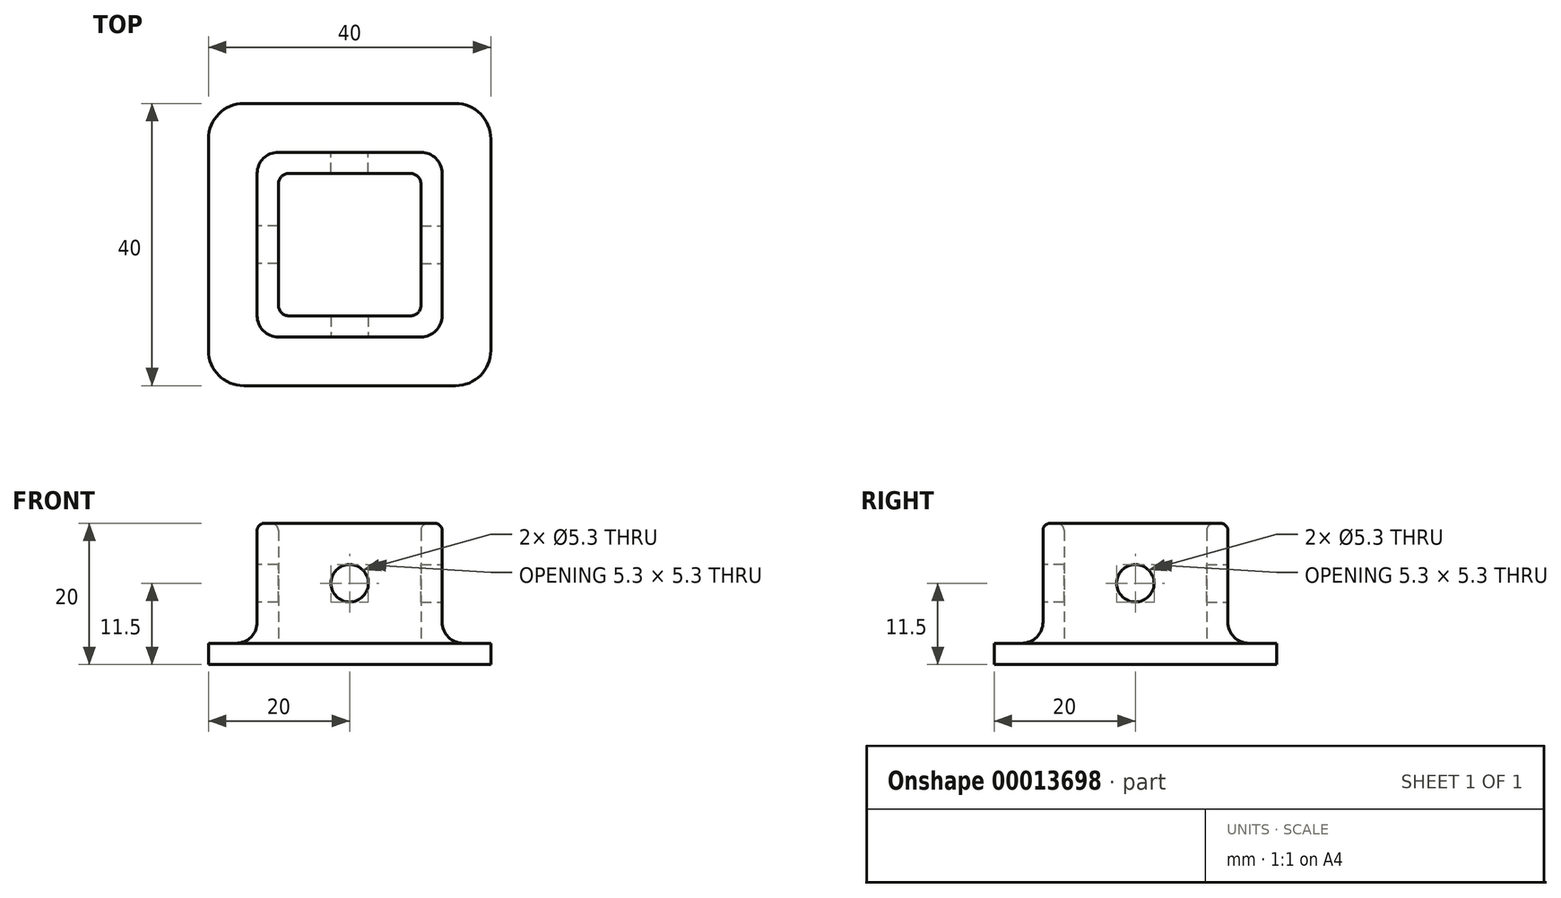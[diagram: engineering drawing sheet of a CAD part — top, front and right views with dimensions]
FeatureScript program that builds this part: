
annotation { "Feature Type Name" : "Feature", "Feature Type Description" : "" }
export const myFeature = defineFeature(function(context is Context, id is Id, definition is map)
    precondition{}
    {
        {
            var Q0;
            Q0=qCreatedBy(makeId("Top.planeOp"),FACE);
            var sketch = newSketch(context, id + "F0", { "sketchPlane" : qUnion([Q0])});
            skLineSegment(sketch, "E0.rect.bottom", {"start": v(10.1, 10.1) * mm, "end": v(-10.1, 10.1) * mm});
            skLineSegment(sketch, "E0.rect.top", {"start": v(10.1, -10.1) * mm, "end": v(-10.1, -10.1) * mm});
            skLineSegment(sketch, "E0.rect.left", {"start": v(10.1, 10.1) * mm, "end": v(10.1, -10.1) * mm});
            skLineSegment(sketch, "E0.rect.right", {"start": v(-10.1, 10.1) * mm, "end": v(-10.1, -10.1) * mm});
            skPoint(sketch, "E0.rect.middle", {"position": v(0, 0) * mm});
            skLineSegment(sketch, "E1.rect.bottom", {"start": v(20, 20) * mm, "end": v(-20, 20) * mm});
            skLineSegment(sketch, "E1.rect.top", {"start": v(20, -20) * mm, "end": v(-20, -20) * mm});
            skLineSegment(sketch, "E1.rect.left", {"start": v(20, 20) * mm, "end": v(20, -20) * mm});
            skLineSegment(sketch, "E1.rect.right", {"start": v(-20, 20) * mm, "end": v(-20, -20) * mm});
            skLineSegment(sketch, "E2.rect.bottom", {"start": v(13.1, 13.1) * mm, "end": v(-13.1, 13.1) * mm});
            skLineSegment(sketch, "E2.rect.top", {"start": v(13.1, -13.1) * mm, "end": v(-13.1, -13.1) * mm});
            skLineSegment(sketch, "E2.rect.left", {"start": v(13.1, 13.1) * mm, "end": v(13.1, -13.1) * mm});
            skLineSegment(sketch, "E2.rect.right", {"start": v(-13.1, 13.1) * mm, "end": v(-13.1, -13.1) * mm});
            skSolve(sketch);
        }
        {
            var Q0;
            Q0=makeQuery(id+"F0.imprint","IMPRINT",FACE,{"disambiguationData":[TD([[makeQuery(id+"F0.imprint","IMPRINT",EDGE,{"derivedFrom":sQuery(id+"F0.wireOp",EDGE,"E1.rect.bottom")}),1.0]])]});
            var Q1;
            Q1=makeQuery(id+"F0.imprint","IMPRINT",FACE,{"disambiguationData":[TD([[makeQuery(id+"F0.imprint","IMPRINT",EDGE,{"derivedFrom":sQuery(id+"F0.wireOp",EDGE,"E0.rect.bottom")}),-1.0]])]});
            var Q2;
            Q2=makeQuery(id+"F0.imprint","IMPRINT",FACE,{"disambiguationData":[TD([[makeQuery(id+"F0.imprint","IMPRINT",EDGE,{"derivedFrom":sQuery(id+"F0.wireOp",EDGE,"E0.rect.bottom")}),1.0]])]});
            extrude(context, id + "F1", {"entities" : qUnion([Q0, Q1, Q2]), "depth" : 3 * mm});
        }
        {
            var Q0;
            Q0=makeQuery(id+"F0.imprint","IMPRINT",FACE,{"disambiguationData":[TD([[makeQuery(id+"F0.imprint","IMPRINT",EDGE,{"derivedFrom":sQuery(id+"F0.wireOp",EDGE,"E0.rect.bottom")}),-1.0]])]});
            extrude(context, id + "F2", {"entities" : qUnion([Q0]), "operationType" : NewBodyOperationType.ADD, "depth" : 20 * mm});
        }
        {
            var Q0;
            Q0=makeQuery(id+"F2.opExtrude","SWEPT_EDGE",EDGE,{"disambiguationData":[OSD([sQuery(id+"F0.wireOp",EDGE,"E0.rect.bottom"),sQuery(id+"F0.wireOp",EDGE,"E0.rect.right")])]});
            var Q1;
            Q1=makeQuery(id+"F2.opExtrude","SWEPT_EDGE",EDGE,{"disambiguationData":[OSD([sQuery(id+"F0.wireOp",EDGE,"E0.rect.bottom"),sQuery(id+"F0.wireOp",EDGE,"E0.rect.left")])]});
            var Q2;
            Q2=makeQuery(id+"F2.opExtrude","SWEPT_EDGE",EDGE,{"disambiguationData":[OSD([sQuery(id+"F0.wireOp",EDGE,"E0.rect.top"),sQuery(id+"F0.wireOp",EDGE,"E0.rect.left")])]});
            var Q3;
            Q3=makeQuery(id+"F2.opExtrude","SWEPT_EDGE",EDGE,{"disambiguationData":[OSD([sQuery(id+"F0.wireOp",EDGE,"E0.rect.top"),sQuery(id+"F0.wireOp",EDGE,"E0.rect.right")])]});
            fillet(context, id + "F3", {"entities" : qUnion([Q0, Q1, Q2, Q3]), "radius" : 1.5 * mm, "tangentPropagation" : true, "allowEdgeOverflow" : false});
        }
        {
            var Q0;
            Q0=makeQuery(id+"F2.opExtrude","SWEPT_FACE",FACE,{"disambiguationData":[OSD([sQuery(id+"F0.wireOp",EDGE,"E2.rect.right")])]});
            var sketch = newSketch(context, id + "F4", { "sketchPlane" : qUnion([Q0])});
            skLineSegment(sketch, "E3", {"start": v(13.1, 11.5) * mm, "end": v(-13.1, 11.5) * mm, "construction": true});
            skCircle(sketch, "E4", {"center": v(0, 11.5) * mm, "radius": 2.65 * mm});
            skSolve(sketch);
        }
        {
            var Q0;
            Q0=makeQuery(id+"F4.imprint","IMPRINT",FACE,{"disambiguationData":[TD([[makeQuery(id+"F4.imprint","IMPRINT",EDGE,{"derivedFrom":sQuery(id+"F4.wireOp",EDGE,"E4")}),1.0]])]});
            extrude(context, id + "F5", {"entities" : qUnion([Q0]), "oppositeDirection" : true, "depth" : 5 * mm});
        }
        {
            var Q0;
            Q0=qCreatedBy(makeId("Front.planeOp"),FACE);
            var sketch = newSketch(context, id + "F6", { "sketchPlane" : qUnion([Q0])});
            skLineSegment(sketch, "E5", {"start": v(0, 0) * mm, "end": v(0, 50) * mm, "construction": true});
            skSolve(sketch);
        }
        {
            var Q0;
            Q0=makeQuery(id+"F5.opExtrude","SWEPT_BODY",BODY,{"disambiguationData":[OSD([sQuery(id+"F4.wireOp",EDGE,"E4")])]});
            var Q1;
            Q1=sQuery(id+"F6.wireOp",EDGE,"E5");
            circularPattern(context, id + "F7", {"entities" : qUnion([Q0]), "axis" : qUnion([Q1]), "angle" : 90 * degree, "instanceCount" : round(4)});
        }
        {
            var Q0;
            Q0=makeQuery(id+"F7.opPattern","COPY",BODY,{"derivedFrom":makeQuery(id+"F5.opExtrude","SWEPT_BODY",BODY,{"disambiguationData":[OSD([sQuery(id+"F4.wireOp",EDGE,"E4")])]}),"instanceName":"2"});
            var Q1;
            Q1=makeQuery(id+"F7.opPattern","COPY",BODY,{"derivedFrom":makeQuery(id+"F5.opExtrude","SWEPT_BODY",BODY,{"disambiguationData":[OSD([sQuery(id+"F4.wireOp",EDGE,"E4")])]}),"instanceName":"3"});
            var Q2;
            Q2=makeQuery(id+"F7.opPattern","COPY",BODY,{"derivedFrom":makeQuery(id+"F5.opExtrude","SWEPT_BODY",BODY,{"disambiguationData":[OSD([sQuery(id+"F4.wireOp",EDGE,"E4")])]}),"instanceName":"1"});
            var Q3;
            Q3=makeQuery(id+"F5.opExtrude","SWEPT_BODY",BODY,{"disambiguationData":[OSD([sQuery(id+"F4.wireOp",EDGE,"E4")])]});
            var Q4;
            Q4=makeQuery(id+"F1.opExtrude","SWEPT_BODY",BODY,{"disambiguationData":[OSD([sQuery(id+"F0.wireOp",EDGE,"E1.rect.bottom"),sQuery(id+"F0.wireOp",EDGE,"E1.rect.top"),sQuery(id+"F0.wireOp",EDGE,"E1.rect.left"),sQuery(id+"F0.wireOp",EDGE,"E1.rect.right")])]});
            booleanBodies(context, id + "F8", {"operationType" : BooleanOperationType.SUBTRACTION, "tools" : qUnion([Q0, Q1, Q2, Q3]), "targets" : qUnion([Q4])});
        }
        {
            var Q0;
            Q0=makeQuery(id+"F2.boolean.opBoolean","INTERSECT",EDGE,{"derivedFrom":[makeQuery(id+"F1.opExtrude","CAP_FACE",FACE,{"disambiguationData":[OSD([sQuery(id+"F0.wireOp",EDGE,"E1.rect.bottom"),sQuery(id+"F0.wireOp",EDGE,"E1.rect.top"),sQuery(id+"F0.wireOp",EDGE,"E1.rect.left"),sQuery(id+"F0.wireOp",EDGE,"E1.rect.right")])],"isStart":false}),makeQuery(id+"F2.opExtrude","SWEPT_FACE",FACE,{"disambiguationData":[OSD([sQuery(id+"F0.wireOp",EDGE,"E2.rect.top")])]})]});
            var Q1;
            Q1=makeQuery(id+"F2.boolean.opBoolean","INTERSECT",EDGE,{"derivedFrom":[makeQuery(id+"F1.opExtrude","CAP_FACE",FACE,{"disambiguationData":[OSD([sQuery(id+"F0.wireOp",EDGE,"E1.rect.bottom"),sQuery(id+"F0.wireOp",EDGE,"E1.rect.top"),sQuery(id+"F0.wireOp",EDGE,"E1.rect.left"),sQuery(id+"F0.wireOp",EDGE,"E1.rect.right")])],"isStart":false}),makeQuery(id+"F2.opExtrude","SWEPT_FACE",FACE,{"disambiguationData":[OSD([sQuery(id+"F0.wireOp",EDGE,"E2.rect.right")])]})]});
            var Q2;
            Q2=makeQuery(id+"F2.boolean.opBoolean","INTERSECT",EDGE,{"derivedFrom":[makeQuery(id+"F1.opExtrude","CAP_FACE",FACE,{"disambiguationData":[OSD([sQuery(id+"F0.wireOp",EDGE,"E1.rect.bottom"),sQuery(id+"F0.wireOp",EDGE,"E1.rect.top"),sQuery(id+"F0.wireOp",EDGE,"E1.rect.left"),sQuery(id+"F0.wireOp",EDGE,"E1.rect.right")])],"isStart":false}),makeQuery(id+"F2.opExtrude","SWEPT_FACE",FACE,{"disambiguationData":[OSD([sQuery(id+"F0.wireOp",EDGE,"E2.rect.bottom")])]})]});
            var Q3;
            Q3=makeQuery(id+"F2.boolean.opBoolean","INTERSECT",EDGE,{"derivedFrom":[makeQuery(id+"F1.opExtrude","CAP_FACE",FACE,{"disambiguationData":[OSD([sQuery(id+"F0.wireOp",EDGE,"E1.rect.bottom"),sQuery(id+"F0.wireOp",EDGE,"E1.rect.top"),sQuery(id+"F0.wireOp",EDGE,"E1.rect.left"),sQuery(id+"F0.wireOp",EDGE,"E1.rect.right")])],"isStart":false}),makeQuery(id+"F2.opExtrude","SWEPT_FACE",FACE,{"disambiguationData":[OSD([sQuery(id+"F0.wireOp",EDGE,"E2.rect.left")])]})]});
            var Q4;
            Q4=makeQuery(id+"F2.opExtrude","SWEPT_EDGE",EDGE,{"disambiguationData":[OSD([sQuery(id+"F0.wireOp",EDGE,"E2.rect.bottom"),sQuery(id+"F0.wireOp",EDGE,"E2.rect.right")])]});
            var Q5;
            Q5=makeQuery(id+"F2.opExtrude","SWEPT_EDGE",EDGE,{"disambiguationData":[OSD([sQuery(id+"F0.wireOp",EDGE,"E2.rect.top"),sQuery(id+"F0.wireOp",EDGE,"E2.rect.right")])]});
            var Q6;
            Q6=makeQuery(id+"F2.opExtrude","SWEPT_EDGE",EDGE,{"disambiguationData":[OSD([sQuery(id+"F0.wireOp",EDGE,"E2.rect.top"),sQuery(id+"F0.wireOp",EDGE,"E2.rect.left")])]});
            var Q7;
            Q7=makeQuery(id+"F2.opExtrude","SWEPT_EDGE",EDGE,{"disambiguationData":[OSD([sQuery(id+"F0.wireOp",EDGE,"E2.rect.bottom"),sQuery(id+"F0.wireOp",EDGE,"E2.rect.left")])]});
            fillet(context, id + "F9", {"entities" : qUnion([Q0, Q1, Q2, Q3, Q4, Q5, Q6, Q7]), "radius" : 3 * mm, "tangentPropagation" : true, "allowEdgeOverflow" : false});
        }
        {
            var Q0;
            Q0=makeQuery(id+"F1.opExtrude","SWEPT_EDGE",EDGE,{"disambiguationData":[OSD([sQuery(id+"F0.wireOp",EDGE,"E1.rect.top"),sQuery(id+"F0.wireOp",EDGE,"E1.rect.right")])]});
            var Q1;
            Q1=makeQuery(id+"F1.opExtrude","SWEPT_EDGE",EDGE,{"disambiguationData":[OSD([sQuery(id+"F0.wireOp",EDGE,"E1.rect.bottom"),sQuery(id+"F0.wireOp",EDGE,"E1.rect.right")])]});
            var Q2;
            Q2=makeQuery(id+"F1.opExtrude","SWEPT_EDGE",EDGE,{"disambiguationData":[OSD([sQuery(id+"F0.wireOp",EDGE,"E1.rect.bottom"),sQuery(id+"F0.wireOp",EDGE,"E1.rect.left")])]});
            var Q3;
            Q3=makeQuery(id+"F1.opExtrude","SWEPT_EDGE",EDGE,{"disambiguationData":[OSD([sQuery(id+"F0.wireOp",EDGE,"E1.rect.top"),sQuery(id+"F0.wireOp",EDGE,"E1.rect.left")])]});
            fillet(context, id + "F10", {"entities" : qUnion([Q0, Q1, Q2, Q3]), "radius" : 5 * mm, "tangentPropagation" : true, "allowEdgeOverflow" : false});
        }
        {
            var Q0;
            Q0=makeQuery(id+"F2.opExtrude","CAP_EDGE",EDGE,{"disambiguationData":[OSD([sQuery(id+"F0.wireOp",EDGE,"E0.rect.right")])],"isStart":false});
            var Q1;
            Q1=makeQuery(id+"F2.opExtrude","CAP_EDGE",EDGE,{"disambiguationData":[OSD([sQuery(id+"F0.wireOp",EDGE,"E2.rect.right")])],"isStart":false});
            fillet(context, id + "F11", {"entities" : qUnion([Q0, Q1]), "radius" : 1 * mm, "tangentPropagation" : true, "allowEdgeOverflow" : false});
        }
    });
